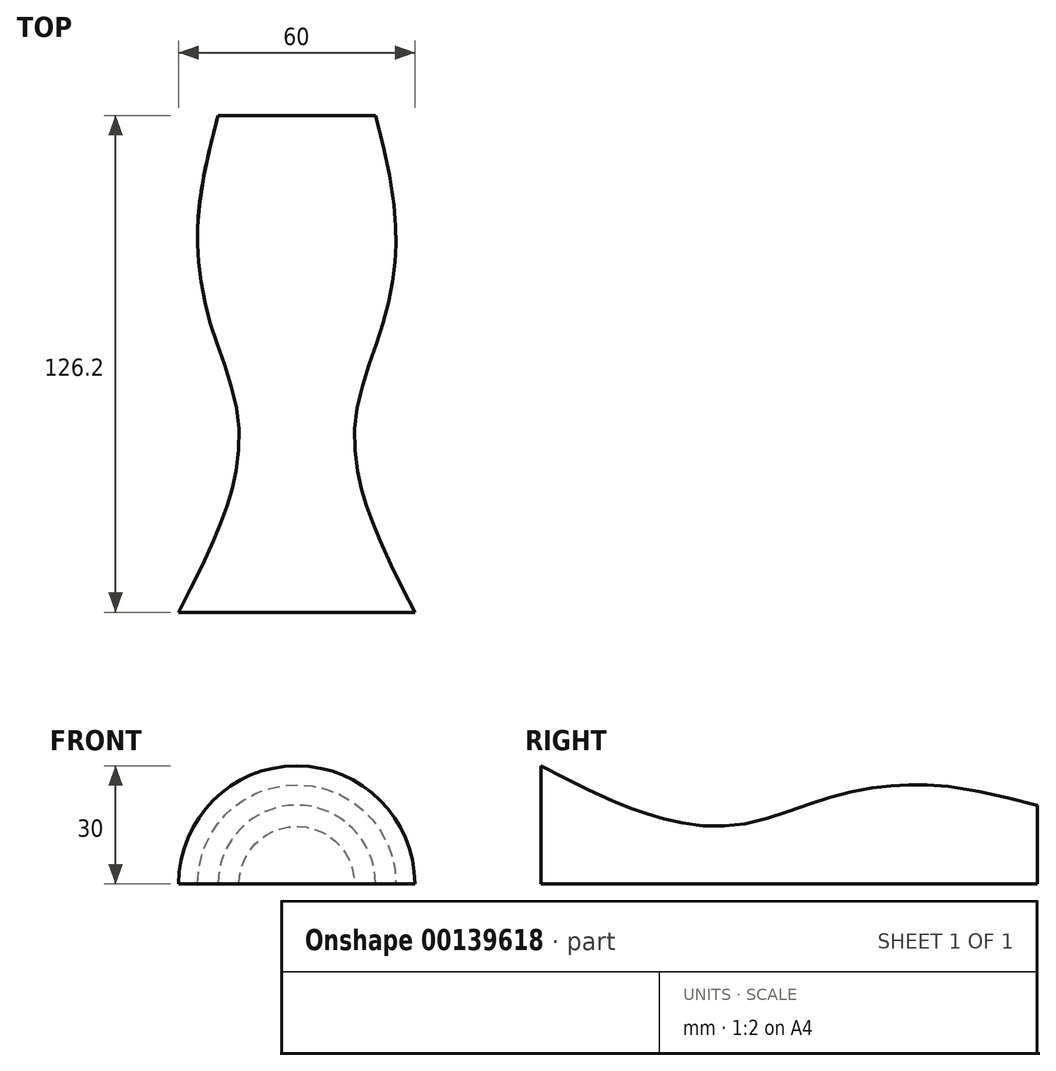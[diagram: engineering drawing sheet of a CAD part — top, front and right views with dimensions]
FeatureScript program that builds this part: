
annotation { "Feature Type Name" : "Feature", "Feature Type Description" : "" }
export const myFeature = defineFeature(function(context is Context, id is Id, definition is map)
    precondition{}
    {
        {
            var Q0;
            Q0=qCreatedBy(makeId("Front.planeOp"),FACE);
            var sketch = newSketch(context, id + "F0", { "sketchPlane" : qUnion([Q0])});
            skCircle(sketch, "E0", {"center": v(0, 0) * mm, "radius": 20 * mm});
            skSolve(sketch);
        }
        {
            var Q0;
            Q0=qCreatedBy(makeId("Front.planeOp"),FACE);
            cPlane(context, id + "F1", {"entities" : qUnion([Q0]), "cplaneType" : CPlaneType.OFFSET, "offset" : 25.4 * mm, "width" : 152.4 * mm, "height" : 152.4 * mm});
        }
        {
            var Q0;
            Q0=qCreatedBy(id+"F1.planeOp",FACE);
            var sketch = newSketch(context, id + "F2", { "sketchPlane" : qUnion([Q0])});
            skCircle(sketch, "E1", {"center": v(0, 0) * mm, "radius": 25 * mm});
            skSolve(sketch);
        }
        {
            var Q0;
            Q0=qCreatedBy(id+"F1.planeOp",FACE);
            cPlane(context, id + "F3", {"entities" : qUnion([Q0]), "cplaneType" : CPlaneType.OFFSET, "offset" : 25.4 * mm, "width" : 152.4 * mm, "height" : 152.4 * mm});
        }
        {
            var Q0;
            Q0=qCreatedBy(id+"F3.planeOp",FACE);
            var sketch = newSketch(context, id + "F4", { "sketchPlane" : qUnion([Q0])});
            skCircle(sketch, "E2", {"center": v(0, 0) * mm, "radius": 22.5 * mm});
            skSolve(sketch);
        }
        {
            var Q0;
            Q0=qCreatedBy(id+"F3.planeOp",FACE);
            cPlane(context, id + "F5", {"entities" : qUnion([Q0]), "cplaneType" : CPlaneType.OFFSET, "offset" : 25.4 * mm, "width" : 152.4 * mm, "height" : 152.4 * mm});
        }
        {
            var Q0;
            Q0=qCreatedBy(id+"F5.planeOp",FACE);
            var sketch = newSketch(context, id + "F6", { "sketchPlane" : qUnion([Q0])});
            skCircle(sketch, "E3", {"center": v(0, 0) * mm, "radius": 15 * mm});
            skSolve(sketch);
        }
        {
            var Q0;
            Q0=qCreatedBy(id+"F5.planeOp",FACE);
            cPlane(context, id + "F7", {"entities" : qUnion([Q0]), "cplaneType" : CPlaneType.OFFSET, "offset" : 50 * mm, "width" : 150 * mm, "height" : 150 * mm});
        }
        {
            var Q0;
            Q0=qCreatedBy(id+"F7.planeOp",FACE);
            var sketch = newSketch(context, id + "F8", { "sketchPlane" : qUnion([Q0])});
            skCircle(sketch, "E4", {"center": v(0, 0) * mm, "radius": 30 * mm});
            skSolve(sketch);
        }
        {
            var Q0;
            Q0 = qSketchRegion(id + "F0", true);
            var Q1;
            Q1 = qSketchRegion(id + "F2", true);
            var Q2;
            Q2 = qSketchRegion(id + "F4", true);
            var Q3;
            Q3 = qSketchRegion(id + "F6", true);
            var Q4;
            Q4=makeQuery(id+"F8.imprint","IMPRINT",FACE,{"disambiguationData":[TD([[makeQuery(id+"F8.imprint","IMPRINT",EDGE,{"derivedFrom":sQuery(id+"F8.wireOp",EDGE,"E4")}),1.0]])]});
            loft(context, id + "F9", {"sheetProfilesArray" : [{ "sheetProfileEntities" : qUnion([Q0]) }, { "sheetProfileEntities" : qUnion([Q1]) }, { "sheetProfileEntities" : qUnion([Q2]) }, { "sheetProfileEntities" : qUnion([Q3]) }, { "sheetProfileEntities" : qUnion([Q4]) }]});
        }
        {
            var Q0;
            Q0=makeQuery(id+"F9.opLoft","CAP_FACE",FACE,{"disambiguationData":[OSD([makeQuery(id+"F8.imprint","IMPRINT",FACE,{"disambiguationData":[TD([[makeQuery(id+"F8.imprint","IMPRINT",EDGE,{"derivedFrom":sQuery(id+"F8.wireOp",EDGE,"E4")}),1.0]])]})])],"isStart":true});
            var sketch = newSketch(context, id + "F10", { "sketchPlane" : qUnion([Q0])});
            skLineSegment(sketch, "E5.bottom", {"start": v(-38.23, 0) * mm, "end": v(40.46, 0) * mm});
            skLineSegment(sketch, "E5.top", {"start": v(-38.23, -33.45) * mm, "end": v(40.46, -33.45) * mm});
            skLineSegment(sketch, "E5.left", {"start": v(-38.23, 0) * mm, "end": v(-38.23, -33.45) * mm});
            skLineSegment(sketch, "E5.right", {"start": v(40.46, 0) * mm, "end": v(40.46, -33.45) * mm});
            skSolve(sketch);
        }
        {
            var Q0;
            Q0 = qSketchRegion(id + "F10", true);
            extrude(context, id + "F11", {"entities" : qUnion([Q0]), "operationType" : NewBodyOperationType.REMOVE, "endBound" : BoundingType.THROUGH_ALL, "oppositeDirection" : true, "depth" : 25.4 * mm});
        }
    });
